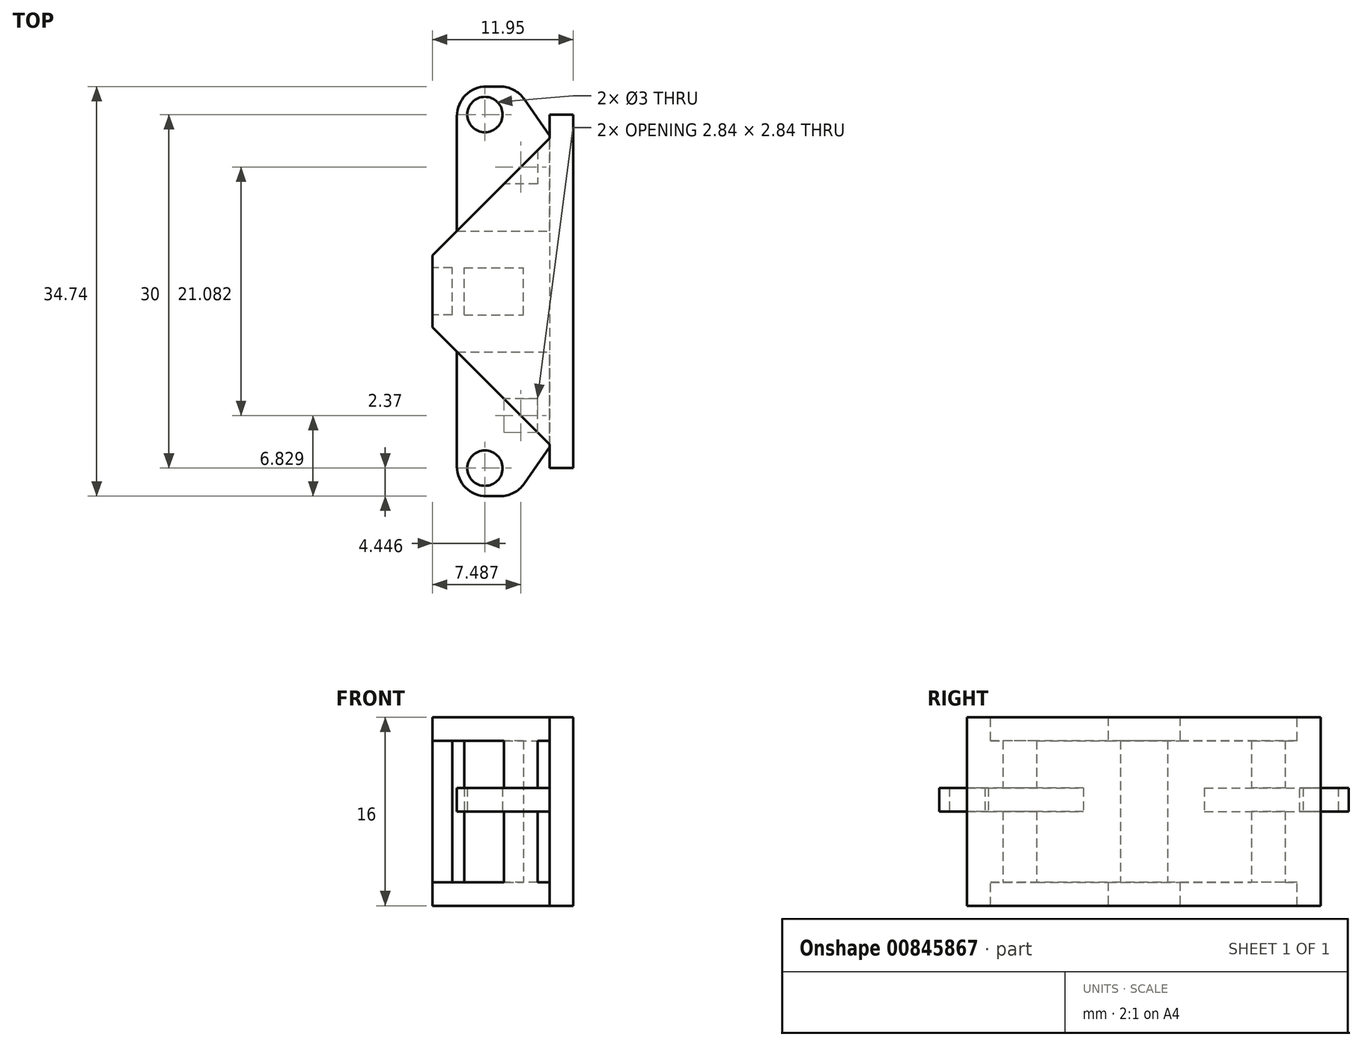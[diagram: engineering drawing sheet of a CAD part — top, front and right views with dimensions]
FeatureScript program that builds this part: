
annotation { "Feature Type Name" : "Feature", "Feature Type Description" : "" }
export const myFeature = defineFeature(function(context is Context, id is Id, definition is map)
    precondition{}
    {
        {
            var Q0;
            Q0=qCreatedBy(makeId("Top.planeOp"),FACE);
            var sketch = newSketch(context, id + "F0", { "sketchPlane" : qUnion([Q0])});
            skLineSegment(sketch, "E0", {"start": v(6.29, 0) * mm, "end": v(6.29, 30) * mm});
            skLineSegment(sketch, "E1", {"start": v(6.29, 30) * mm, "end": v(-8.71, 15) * mm});
            skLineSegment(sketch, "E2", {"start": v(-8.71, 15) * mm, "end": v(-8.71, 15) * mm});
            skLineSegment(sketch, "E3", {"start": v(-8.71, 15) * mm, "end": v(6.29, 0) * mm});
            skLineSegment(sketch, "E4", {"start": v(-8.71, 15) * mm, "end": v(6.29, 15) * mm, "construction": true});
            skLineSegment(sketch, "E5", {"start": v(-5.66, 18.05) * mm, "end": v(-5.66, 11.95) * mm});
            skSolve(sketch);
        }
        {
            var Q0;
            {var subQ0=sQuery(id+"F0.wireOp",EDGE,"E0");Q0=makeQuery(id+"F0.imprint","IMPRINT",FACE,{"disambiguationData":[TD([[makeQuery(id+"F0.imprint","IMPRINT",EDGE,{"derivedFrom":subQ0}),1.0]])]});}
            extrude(context, id + "F1", {"entities" : qUnion([Q0]), "depth" : 8 * mm, "offsetDistance" : 25 * mm, "hasSecondDirection" : true, "secondDirectionOppositeDirection" : true, "secondDirectionDepth" : 8 * mm});
        }
        {
            var Q0;
            Q0=qCreatedBy(makeId("Front.planeOp"),FACE);
            var sketch = newSketch(context, id + "F2", { "sketchPlane" : qUnion([Q0])});
            skLineSegment(sketch, "E6.0", {"start": v(-8.71, 8) * mm, "end": v(-8.71, -8) * mm, "construction": true});
            skLineSegment(sketch, "E7.0", {"start": v(-8.71, 8) * mm, "end": v(6.29, 8) * mm, "construction": true});
            skLineSegment(sketch, "E8.0", {"start": v(6.29, 8) * mm, "end": v(6.29, -8) * mm, "construction": true});
            skLineSegment(sketch, "E9.0", {"start": v(-8.71, -8) * mm, "end": v(6.29, -8) * mm, "construction": true});
            skLineSegment(sketch, "E10.0", {"start": v(-6.71, 6) * mm, "end": v(-6.71, -6) * mm});
            skLineSegment(sketch, "E10.1", {"start": v(-6.71, 6) * mm, "end": v(4.29, 6) * mm});
            skLineSegment(sketch, "E10.2", {"start": v(4.29, 6) * mm, "end": v(4.29, -6) * mm});
            skLineSegment(sketch, "E10.3", {"start": v(-6.71, -6) * mm, "end": v(4.29, -6) * mm});
            skSolve(sketch);
        }
        {
            var Q0;
            Q0 = qSketchRegion(id + "F2", true);
            extrude(context, id + "F3", {"entities" : qUnion([Q0]), "operationType" : NewBodyOperationType.REMOVE, "endBound" : BoundingType.THROUGH_ALL, "oppositeDirection" : true, "depth" : 25 * mm, "offsetDistance" : 25 * mm});
        }
        {
            var Q0;
            Q0=qCreatedBy(makeId("Top.planeOp"),FACE);
            var sketch = newSketch(context, id + "F4", { "sketchPlane" : qUnion([Q0])});
            skLineSegment(sketch, "E11.0", {"start": v(4.37, 1.91) * mm, "end": v(6.29, 0) * mm, "construction": true});
            skLineSegment(sketch, "E12.0", {"start": v(6.29, 30) * mm, "end": v(-8.71, 15) * mm, "construction": true});
            skLineSegment(sketch, "E13.0", {"start": v(6.29, 0) * mm, "end": v(6.29, 0) * mm});
            skLineSegment(sketch, "E14.bottom", {"start": v(-3.59, 9.87) * mm, "end": v(4.37, 9.87) * mm});
            skLineSegment(sketch, "E14.top", {"start": v(-3.59, -2.37) * mm, "end": v(1.37, -2.37) * mm});
            skLineSegment(sketch, "E14.left", {"start": v(-3.59, 9.87) * mm, "end": v(-3.59, -2.37) * mm});
            skLineSegment(sketch, "E14.right", {"start": v(4.37, 9.87) * mm, "end": v(4.37, 1.91) * mm});
            skCircle(sketch, "E15", {"center": v(-1.21, 0) * mm, "radius": 1.5 * mm});
            skPoint(sketch, "E15.centerSnap0", {"position": v(1.35, -3.44) * mm});
            skLineSegment(sketch, "E16", {"start": v(-1.21, 15) * mm, "end": v(-1.21, -2.83) * mm, "construction": true});
            skPoint(sketch, "E17.MirrorP", {"position": v(1.35, 3.44) * mm});
            skPoint(sketch, "E18.orphan", {"position": v(4.37, -2.37) * mm});
            skPoint(sketch, "E19.orphan", {"position": v(4.37, 2.37) * mm});
            skLineSegment(sketch, "E20.MirrorCS", {"start": v(1.37, -2.37) * mm, "end": v(4.37, 1.91) * mm});
            skLineSegment(sketch, "E21.0", {"start": v(6.29, 0) * mm, "end": v(6.29, 30) * mm, "construction": true});
            skLineSegment(sketch, "E22", {"start": v(6.29, 15) * mm, "end": v(-4.86, 15) * mm, "construction": true});
            skCircle(sketch, "E23.MirrorC", {"center": v(-1.21, 30) * mm, "radius": 1.5 * mm});
            skPoint(sketch, "E24.MirrorP", {"position": v(1.35, 26.56) * mm});
            skLineSegment(sketch, "E25.MirrorCS", {"start": v(4.37, 20.13) * mm, "end": v(4.37, 28.09) * mm});
            skLineSegment(sketch, "E26.MirrorCS", {"start": v(1.37, 32.37) * mm, "end": v(4.37, 28.09) * mm});
            skLineSegment(sketch, "E27.MirrorCS", {"start": v(-3.59, 20.13) * mm, "end": v(-3.59, 32.37) * mm});
            skLineSegment(sketch, "E28.MirrorCS", {"start": v(-3.59, 20.13) * mm, "end": v(4.37, 20.13) * mm});
            skPoint(sketch, "E29.MirrorP", {"position": v(4.37, 27.63) * mm});
            skLineSegment(sketch, "E30.MirrorCS", {"start": v(-3.59, 32.37) * mm, "end": v(1.37, 32.37) * mm});
            skPoint(sketch, "E31.MirrorP", {"position": v(4.37, 32.37) * mm});
            skSolve(sketch);
        }
        {
            var Q0;
            Q0 = qSketchRegion(id + "F4", true);
            extrude(context, id + "F5", {"entities" : qUnion([Q0]), "operationType" : NewBodyOperationType.ADD, "depth" : 2 * mm, "offsetDistance" : 25 * mm});
        }
        {
            var Q0;
            Q0=makeQuery(id+"F5.opExtrude","SWEPT_EDGE",EDGE,{"disambiguationData":[OSD([sQuery(id+"F4.wireOp",EDGE,"E14.top"),sQuery(id+"F4.wireOp",EDGE,"E14.left")])]});
            var Q1;
            Q1=makeQuery(id+"F5.opExtrude","SWEPT_EDGE",EDGE,{"disambiguationData":[OSD([sQuery(id+"F4.wireOp",EDGE,"E14.top"),sQuery(id+"F4.wireOp",EDGE,"E20.MirrorCS")])]});
            var Q2;
            Q2=makeQuery(id+"F5.opExtrude","SWEPT_EDGE",EDGE,{"disambiguationData":[OSD([sQuery(id+"F4.wireOp",EDGE,"E27.MirrorCS"),sQuery(id+"F4.wireOp",EDGE,"E30.MirrorCS")])]});
            var Q3;
            Q3=makeQuery(id+"F5.opExtrude","SWEPT_EDGE",EDGE,{"disambiguationData":[OSD([sQuery(id+"F4.wireOp",EDGE,"E26.MirrorCS"),sQuery(id+"F4.wireOp",EDGE,"E30.MirrorCS")])]});
            fillet(context, id + "F6", {"entities" : qUnion([Q0, Q1, Q2, Q3]), "radius" : 2.5 * mm, "tangentPropagation" : true, "allowEdgeOverflow" : false});
        }
        {
            var Q0;
            Q0=makeQuery(id+"F1.opExtrude","CAP_FACE",FACE,{"disambiguationData":[OSD([sQuery(id+"F0.wireOp",EDGE,"E0"),sQuery(id+"F0.wireOp",EDGE,"E1"),sQuery(id+"F0.wireOp",EDGE,"E3")])],"isStart":false});
            var sketch = newSketch(context, id + "F7", { "sketchPlane" : qUnion([Q0])});
            skLineSegment(sketch, "E32.0", {"start": v(6.29, 0) * mm, "end": v(6.29, 0) * mm});
            skLineSegment(sketch, "E33.0", {"start": v(6.29, 30) * mm, "end": v(-8.71, 15) * mm, "construction": true});
            skLineSegment(sketch, "E34", {"start": v(-8.71, 15) * mm, "end": v(6.29, 15) * mm, "construction": true});
            skLineSegment(sketch, "E35", {"start": v(6.29, 0) * mm, "end": v(4.29, 0) * mm});
            skLineSegment(sketch, "E36", {"start": v(4.29, 0) * mm, "end": v(4.29, 2) * mm});
            skLineSegment(sketch, "E37.MirrorCS", {"start": v(6.29, 30) * mm, "end": v(4.29, 30) * mm});
            skLineSegment(sketch, "E38.MirrorCS", {"start": v(4.29, 30) * mm, "end": v(4.29, 28) * mm});
            skSolve(sketch);
        }
        {
            var Q0;
            {var subQ0=sQuery(id+"F7.wireOp",EDGE,"E35");Q0=makeQuery(id+"F7.imprint","IMPRINT",FACE,{"disambiguationData":[TD([[makeQuery(id+"F7.imprint","IMPRINT",EDGE,{"derivedFrom":subQ0}),-1.0]])]});}
            var Q1;
            {var subQ0=sQuery(id+"F7.wireOp",EDGE,"E37.MirrorCS");Q1=makeQuery(id+"F7.imprint","IMPRINT",FACE,{"disambiguationData":[TD([[makeQuery(id+"F7.imprint","IMPRINT",EDGE,{"derivedFrom":subQ0}),1.0]])]});}
            var Q2;
            Q2=makeQuery(id+"F1.opExtrude","CAP_FACE",FACE,{"disambiguationData":[OSD([sQuery(id+"F0.wireOp",EDGE,"E0"),sQuery(id+"F0.wireOp",EDGE,"E1"),sQuery(id+"F0.wireOp",EDGE,"E3")])],"isStart":true});
            extrude(context, id + "F8", {"entities" : qUnion([Q0, Q1]), "operationType" : NewBodyOperationType.ADD, "endBound" : BoundingType.UP_TO_SURFACE, "oppositeDirection" : true, "depth" : 25 * mm, "endBoundEntityFace" : qUnion([Q2]), "offsetDistance" : 25 * mm});
        }
        {
            var Q0;
            Q0=makeQuery(id+"F3.boolean.opBoolean","COPY",FACE,{"derivedFrom":makeQuery(id+"F3.opExtrude","SWEPT_FACE",FACE,{"disambiguationData":[OSD([sQuery(id+"F2.wireOp",EDGE,"E10.3")])]})});
            var sketch = newSketch(context, id + "F9", { "sketchPlane" : qUnion([Q0])});
            skLineSegment(sketch, "E39.bottom", {"start": v(-2.97, 13) * mm, "end": v(2.05, 13) * mm});
            skLineSegment(sketch, "E39.top", {"start": v(-2.97, 17) * mm, "end": v(2.05, 17) * mm});
            skLineSegment(sketch, "E39.left", {"start": v(-2.97, 13) * mm, "end": v(-2.97, 17) * mm});
            skLineSegment(sketch, "E39.right", {"start": v(2.05, 13) * mm, "end": v(2.05, 17) * mm});
            skLineSegment(sketch, "E40.bottom", {"start": v(-3.98, 13) * mm, "end": v(-5.65, 13) * mm});
            skLineSegment(sketch, "E40.top", {"start": v(-3.98, 17) * mm, "end": v(-5.65, 17) * mm});
            skLineSegment(sketch, "E40.left", {"start": v(-3.98, 13) * mm, "end": v(-3.98, 17) * mm});
            skLineSegment(sketch, "E40.right", {"start": v(-5.65, 13) * mm, "end": v(-5.65, 17) * mm});
            skLineSegment(sketch, "E41", {"start": v(3.25, 26.96) * mm, "end": v(3.25, 24.12) * mm});
            skLineSegment(sketch, "E42", {"start": v(3.25, 24.12) * mm, "end": v(0.4, 24.12) * mm});
            skLineSegment(sketch, "E43", {"start": v(0.4, 24.12) * mm, "end": v(3.25, 26.96) * mm});
            skLineSegment(sketch, "E44", {"start": v(-5.65, 15) * mm, "end": v(5.33, 15) * mm, "construction": true});
            skPoint(sketch, "E44.endSnap0", {"position": v(2.05, 15) * mm});
            skLineSegment(sketch, "E45.MirrorCS", {"start": v(3.25, 3.04) * mm, "end": v(3.25, 5.88) * mm});
            skLineSegment(sketch, "E46.MirrorCS", {"start": v(0.4, 5.88) * mm, "end": v(3.25, 3.04) * mm});
            skLineSegment(sketch, "E47.MirrorCS", {"start": v(3.25, 5.88) * mm, "end": v(0.4, 5.88) * mm});
            skSolve(sketch);
        }
        {
            var Q0;
            Q0 = qSketchRegion(id + "F9", true);
            var Q1;
            Q1=makeQuery(id+"F3.boolean.opBoolean","COPY",FACE,{"derivedFrom":makeQuery(id+"F3.opExtrude","SWEPT_FACE",FACE,{"disambiguationData":[OSD([sQuery(id+"F2.wireOp",EDGE,"E10.1")])]})});
            extrude(context, id + "F10", {"entities" : qUnion([Q0]), "operationType" : NewBodyOperationType.ADD, "endBound" : BoundingType.UP_TO_SURFACE, "depth" : 25 * mm, "endBoundEntityFace" : qUnion([Q1]), "offsetDistance" : 25 * mm});
        }
    });
